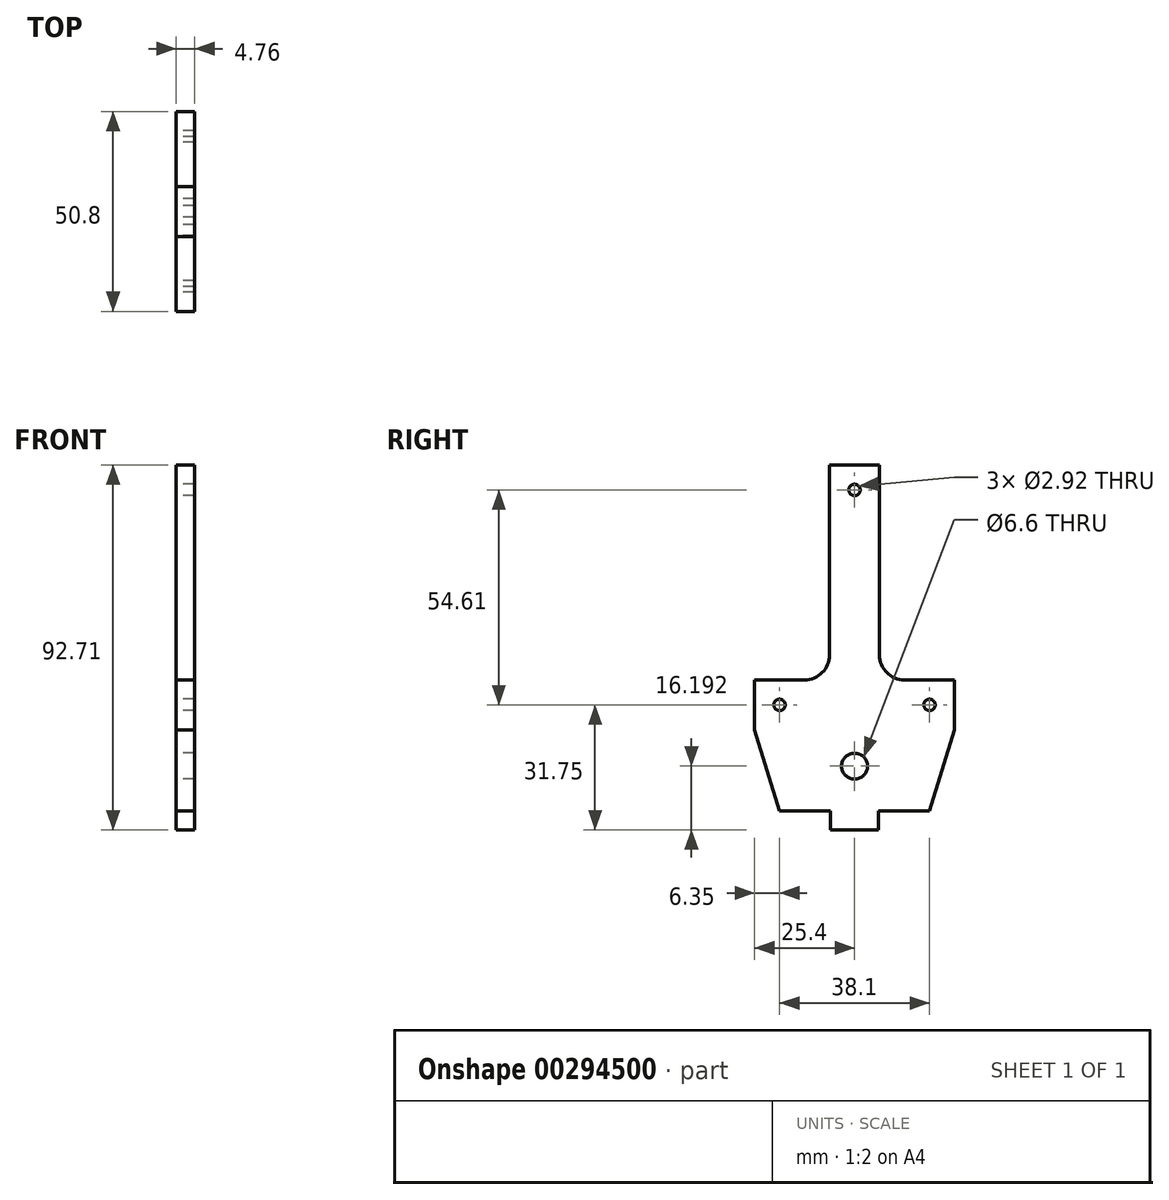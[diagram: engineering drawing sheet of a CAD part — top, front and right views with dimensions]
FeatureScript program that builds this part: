
annotation { "Feature Type Name" : "Feature", "Feature Type Description" : "" }
export const myFeature = defineFeature(function(context is Context, id is Id, definition is map)
    precondition{}
    {
        {
            var Q0;
            Q0=qCreatedBy(makeId("Right.planeOp"),FACE);
            var sketch = newSketch(context, id + "F0", { "sketchPlane" : qUnion([Q0])});
            skLineSegment(sketch, "E0.bottom", {"start": v(0, 0) * mm, "end": v(50.8, 0) * mm, "construction": true});
            skLineSegment(sketch, "E0.top", {"start": v(0, 12.7) * mm, "end": v(12.7, 12.7) * mm});
            skLineSegment(sketch, "E0.left", {"start": v(0, 0) * mm, "end": v(0, 12.7) * mm});
            skLineSegment(sketch, "E0.right", {"start": v(50.8, 0) * mm, "end": v(50.8, 12.7) * mm});
            skLineSegment(sketch, "E1.top", {"start": v(19.05, 67.31) * mm, "end": v(31.75, 67.31) * mm});
            skCircle(sketch, "E2", {"center": v(25.4, 60.96) * mm, "radius": 1.46 * mm});
            skCircle(sketch, "E3", {"center": v(6.35, 6.35) * mm, "radius": 1.46 * mm});
            skCircle(sketch, "E4", {"center": v(44.45, 6.35) * mm, "radius": 1.46 * mm});
            skLineSegment(sketch, "E5", {"start": v(50.8, 6.35) * mm, "end": v(0, 6.35) * mm, "construction": true});
            skLineSegment(sketch, "E6", {"start": v(25.4, 67.31) * mm, "end": v(25.4, 0) * mm, "construction": true});
            skLineSegment(sketch, "E7.trimOffspring", {"start": v(19.05, 19.05) * mm, "end": v(19.05, 67.31) * mm});
            skLineSegment(sketch, "E8.trimOffspring", {"start": v(38.1, 12.7) * mm, "end": v(50.8, 12.7) * mm});
            skLineSegment(sketch, "E9.trimOffspring", {"start": v(31.75, 19.05) * mm, "end": v(31.75, 67.31) * mm});
            skCircle(sketch, "E10", {"center": v(25.4, 60.96) * mm, "radius": 8.26 * mm, "construction": true});
            skCircle(sketch, "E11", {"center": v(44.45, 6.35) * mm, "radius": 8.26 * mm, "construction": true});
            skCircle(sketch, "E12", {"center": v(6.35, 6.35) * mm, "radius": 8.26 * mm, "construction": true});
            skLineSegment(sketch, "E13.bottom", {"start": v(-10.84, 52.7) * mm, "end": v(56.93, 52.7) * mm, "construction": true});
            skLineSegment(sketch, "E13.top", {"start": v(-10.84, 14.6) * mm, "end": v(56.93, 14.6) * mm, "construction": true});
            skLineSegment(sketch, "E13.left", {"start": v(-10.84, 52.7) * mm, "end": v(-10.84, 14.6) * mm, "construction": true});
            skLineSegment(sketch, "E13.right", {"start": v(56.93, 52.7) * mm, "end": v(56.93, 14.6) * mm, "construction": true});
            skPoint(sketch, "E14.visualSharp", {"position": v(19.05, 12.7) * mm});
            skArc(sketch, "E14.filletArc", {"start": v(12.7, 12.7) * mm, "mid": v(17.2, 14.56) * mm, "end": v(19.05, 19.05) * mm});
            skPoint(sketch, "E15.visualSharp", {"position": v(31.75, 12.7) * mm});
            skArc(sketch, "E15.filletArc", {"start": v(31.75, 19.05) * mm, "mid": v(33.6, 14.56) * mm, "end": v(38.1, 12.7) * mm});
            skLineSegment(sketch, "E16.top", {"start": v(6.35, -20.64) * mm, "end": v(19.3, -20.64) * mm});
            skLineSegment(sketch, "E16.right", {"start": v(19.3, -25.4) * mm, "end": v(19.3, -20.64) * mm});
            skLineSegment(sketch, "E17.top", {"start": v(44.45, -20.64) * mm, "end": v(31.5, -20.64) * mm});
            skLineSegment(sketch, "E17.right", {"start": v(31.5, -25.4) * mm, "end": v(31.5, -20.64) * mm});
            skLineSegment(sketch, "E18", {"start": v(19.3, -25.4) * mm, "end": v(31.5, -25.4) * mm});
            skCircle(sketch, "E19", {"center": v(25.4, -9.2) * mm, "radius": 3.3 * mm});
            skLineSegment(sketch, "E20", {"start": v(6.35, -20.64) * mm, "end": v(0, 0) * mm});
            skLineSegment(sketch, "E21", {"start": v(44.45, -20.64) * mm, "end": v(50.8, 0) * mm});
            skSolve(sketch);
        }
        {
            var Q0;
            Q0=makeQuery(id+"F0.imprint","IMPRINT",FACE,{"disambiguationData":[TD([[makeQuery(id+"F0.imprint","IMPRINT",EDGE,{"derivedFrom":sQuery(id+"F0.wireOp",EDGE,"E0.bottom")}),1.0]])]});
            var Q1;
            Q1=makeQuery(id+"F0.imprint","IMPRINT",FACE,{"disambiguationData":[TD([[makeQuery(id+"F0.imprint","IMPRINT",EDGE,{"derivedFrom":sQuery(id+"F0.wireOp",EDGE,"E0.bottom")}),-1.0]])]});
            var Q2;
            Q2=makeQuery(id+"F0.imprint","IMPRINT",FACE,{"disambiguationData":[TD([[makeQuery(id+"F0.imprint","IMPRINT",EDGE,{"derivedFrom":sQuery(id+"F0.wireOp",EDGE,"E0.top")}),-1.0]])]});
            extrude(context, id + "F1", {"entities" : qUnion([Q0, Q1, Q2]), "depth" : 4.76 * mm});
        }
    });
